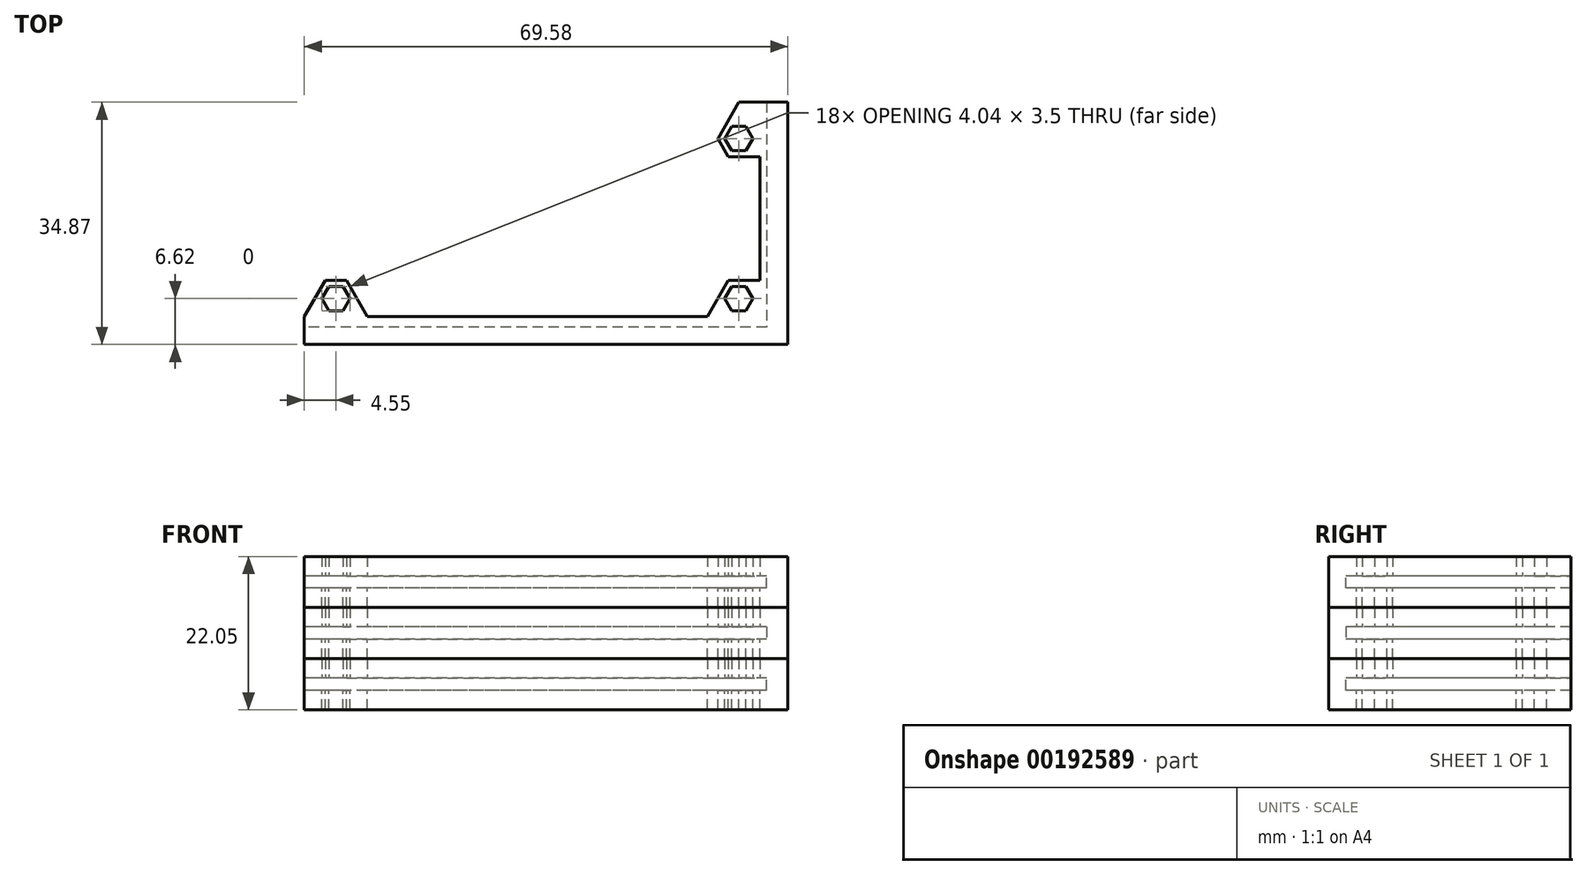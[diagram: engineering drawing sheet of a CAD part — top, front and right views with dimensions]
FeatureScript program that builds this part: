
annotation { "Feature Type Name" : "Feature", "Feature Type Description" : "" }
export const myFeature = defineFeature(function(context is Context, id is Id, definition is map)
    precondition{}
    {
        {
            var Q0;
            Q0=qCreatedBy(makeId("Top.planeOp"),FACE);
            var sketch = newSketch(context, id + "F0", { "sketchPlane" : qUnion([Q0])});
            skLineSegment(sketch, "E0.bottom", {"start": v(-29, 11.5) * mm, "end": v(29, 11.5) * mm, "construction": true});
            skLineSegment(sketch, "E0.top", {"start": v(-29, -11.5) * mm, "end": v(29, -11.5) * mm, "construction": true});
            skLineSegment(sketch, "E0.left", {"start": v(-29, 11.5) * mm, "end": v(-29, -11.5) * mm, "construction": true});
            skLineSegment(sketch, "E0.right", {"start": v(29, 11.5) * mm, "end": v(29, -11.5) * mm, "construction": true});
            skLineSegment(sketch, "E1", {"start": v(0, 11.5) * mm, "end": v(0, -11.5) * mm, "construction": true});
            skCircle(sketch, "E2.cCircle", {"center": v(-29, 11.5) * mm, "radius": 2.62 * mm, "construction": true});
            skLineSegment(sketch, "E2.0", {"start": v(-27.48, 14.12) * mm, "end": v(-25.97, 11.5) * mm});
            skLineSegment(sketch, "E2.1", {"start": v(-25.97, 11.5) * mm, "end": v(-27.48, 8.88) * mm});
            skLineSegment(sketch, "E2.2", {"start": v(-27.48, 8.87) * mm, "end": v(-30.52, 8.87) * mm});
            skLineSegment(sketch, "E2.3", {"start": v(-30.52, 8.88) * mm, "end": v(-32.03, 11.5) * mm});
            skLineSegment(sketch, "E2.4", {"start": v(-32.03, 11.5) * mm, "end": v(-30.52, 14.13) * mm});
            skLineSegment(sketch, "E2.5", {"start": v(-30.52, 14.13) * mm, "end": v(-27.48, 14.13) * mm});
            skLineSegment(sketch, "E3", {"start": v(-29, 0) * mm, "end": v(29, 0) * mm, "construction": true});
            skLineSegment(sketch, "E4.MirrorCS", {"start": v(-27.48, -14.12) * mm, "end": v(-25.97, -11.5) * mm});
            skLineSegment(sketch, "E5.MirrorCS", {"start": v(-25.97, -11.5) * mm, "end": v(-27.48, -8.88) * mm});
            skLineSegment(sketch, "E6.MirrorCS", {"start": v(-27.48, -8.87) * mm, "end": v(-30.52, -8.87) * mm});
            skLineSegment(sketch, "E7.MirrorCS", {"start": v(-30.52, -8.88) * mm, "end": v(-32.03, -11.5) * mm});
            skLineSegment(sketch, "E8.MirrorCS", {"start": v(-30.52, -14.12) * mm, "end": v(-27.48, -14.12) * mm});
            skLineSegment(sketch, "E9.MirrorCS", {"start": v(-32.03, -11.5) * mm, "end": v(-30.52, -14.13) * mm});
            skLineSegment(sketch, "E10.MirrorCS", {"start": v(30.52, -8.87) * mm, "end": v(32.03, -11.5) * mm});
            skLineSegment(sketch, "E11.MirrorCS", {"start": v(32.03, -11.5) * mm, "end": v(30.52, -14.12) * mm});
            skLineSegment(sketch, "E12.MirrorCS", {"start": v(30.52, -14.12) * mm, "end": v(27.48, -14.12) * mm});
            skLineSegment(sketch, "E13.MirrorCS", {"start": v(27.48, -14.12) * mm, "end": v(25.97, -11.5) * mm});
            skLineSegment(sketch, "E14.MirrorCS", {"start": v(25.97, -11.5) * mm, "end": v(27.48, -8.87) * mm});
            skLineSegment(sketch, "E15.MirrorCS", {"start": v(27.48, -8.87) * mm, "end": v(30.52, -8.87) * mm});
            skLineSegment(sketch, "E16.MirrorCS", {"start": v(30.52, 8.87) * mm, "end": v(32.03, 11.5) * mm});
            skLineSegment(sketch, "E17.MirrorCS", {"start": v(32.03, 11.5) * mm, "end": v(30.52, 14.12) * mm});
            skLineSegment(sketch, "E18.MirrorCS", {"start": v(30.52, 14.13) * mm, "end": v(27.48, 14.13) * mm});
            skLineSegment(sketch, "E19.MirrorCS", {"start": v(27.48, 8.88) * mm, "end": v(30.52, 8.88) * mm});
            skLineSegment(sketch, "E20.MirrorCS", {"start": v(27.48, 14.12) * mm, "end": v(25.97, 11.5) * mm});
            skLineSegment(sketch, "E21.MirrorCS", {"start": v(25.97, 11.5) * mm, "end": v(27.48, 8.87) * mm});
            skCircle(sketch, "E22.cCircle", {"center": v(-29, 11.5) * mm, "radius": 1.75 * mm, "construction": true});
            skLineSegment(sketch, "E22.0", {"start": v(-30.01, 13.25) * mm, "end": v(-27.99, 13.25) * mm});
            skLineSegment(sketch, "E22.1", {"start": v(-27.99, 13.25) * mm, "end": v(-26.98, 11.5) * mm});
            skLineSegment(sketch, "E22.2", {"start": v(-26.98, 11.5) * mm, "end": v(-27.99, 9.75) * mm});
            skLineSegment(sketch, "E22.3", {"start": v(-27.99, 9.75) * mm, "end": v(-30.01, 9.75) * mm});
            skLineSegment(sketch, "E22.4", {"start": v(-30.01, 9.75) * mm, "end": v(-31.02, 11.5) * mm});
            skLineSegment(sketch, "E22.5", {"start": v(-31.02, 11.5) * mm, "end": v(-30.01, 13.25) * mm});
            skLineSegment(sketch, "E23.MirrorCS", {"start": v(26.98, 11.5) * mm, "end": v(27.99, 9.75) * mm});
            skLineSegment(sketch, "E24.MirrorCS", {"start": v(27.99, 9.75) * mm, "end": v(30.01, 9.75) * mm});
            skLineSegment(sketch, "E25.MirrorCS", {"start": v(30.01, 9.75) * mm, "end": v(31.02, 11.5) * mm});
            skLineSegment(sketch, "E26.MirrorCS", {"start": v(31.02, 11.5) * mm, "end": v(30.01, 13.25) * mm});
            skLineSegment(sketch, "E27.MirrorCS", {"start": v(30.01, 13.25) * mm, "end": v(27.99, 13.25) * mm});
            skLineSegment(sketch, "E28.MirrorCS", {"start": v(27.99, 13.25) * mm, "end": v(26.98, 11.5) * mm});
            skLineSegment(sketch, "E29.MirrorCS", {"start": v(26.98, -11.5) * mm, "end": v(27.99, -9.75) * mm});
            skLineSegment(sketch, "E30.MirrorCS", {"start": v(27.99, -9.75) * mm, "end": v(30.01, -9.75) * mm});
            skLineSegment(sketch, "E31.MirrorCS", {"start": v(30.01, -9.75) * mm, "end": v(31.02, -11.5) * mm});
            skLineSegment(sketch, "E32.MirrorCS", {"start": v(31.02, -11.5) * mm, "end": v(30.01, -13.25) * mm});
            skLineSegment(sketch, "E33.MirrorCS", {"start": v(30.01, -13.25) * mm, "end": v(27.99, -13.25) * mm});
            skLineSegment(sketch, "E34.MirrorCS", {"start": v(27.99, -13.25) * mm, "end": v(26.98, -11.5) * mm});
            skLineSegment(sketch, "E35.MirrorCS", {"start": v(-31.02, -11.5) * mm, "end": v(-30.01, -13.25) * mm});
            skLineSegment(sketch, "E36.MirrorCS", {"start": v(-30.01, -9.75) * mm, "end": v(-31.02, -11.5) * mm});
            skLineSegment(sketch, "E37.MirrorCS", {"start": v(-27.99, -9.75) * mm, "end": v(-30.01, -9.75) * mm});
            skLineSegment(sketch, "E38.MirrorCS", {"start": v(-26.98, -11.5) * mm, "end": v(-27.99, -9.75) * mm});
            skLineSegment(sketch, "E39.MirrorCS", {"start": v(-30.01, -13.25) * mm, "end": v(-27.99, -13.25) * mm});
            skLineSegment(sketch, "E40.MirrorCS", {"start": v(-27.99, -13.25) * mm, "end": v(-26.98, -11.5) * mm});
            skLineSegment(sketch, "E41.bottom", {"start": v(-32.5, 15.12) * mm, "end": v(32.5, 15.13) * mm});
            skLineSegment(sketch, "E41.top", {"start": v(-32.5, -15.13) * mm, "end": v(32.5, -15.13) * mm});
            skLineSegment(sketch, "E41.left", {"start": v(-32.5, 15.12) * mm, "end": v(-32.5, -15.13) * mm});
            skLineSegment(sketch, "E41.right", {"start": v(32.5, 15.13) * mm, "end": v(32.5, -15.13) * mm});
            skLineSegment(sketch, "E42", {"start": v(32.5, 15.13) * mm, "end": v(-32.5, -15.13) * mm, "construction": true});
            skPoint(sketch, "E43", {"position": v(0, 0) * mm});
            skSolve(sketch);
        }
        {
            var Q0;
            Q0=qCreatedBy(makeId("Top.planeOp"),FACE);
            var sketch = newSketch(context, id + "F1", { "sketchPlane" : qUnion([Q0])});
            skLineSegment(sketch, "E44.0", {"start": v(-30.52, -8.88) * mm, "end": v(-32.03, -11.5) * mm});
            skLineSegment(sketch, "E44.1", {"start": v(-27.48, -8.87) * mm, "end": v(-30.52, -8.87) * mm});
            skLineSegment(sketch, "E44.2", {"start": v(-25.97, -11.5) * mm, "end": v(-27.48, -8.88) * mm});
            skLineSegment(sketch, "E45.0", {"start": v(25.97, -11.5) * mm, "end": v(27.48, -8.87) * mm});
            skLineSegment(sketch, "E45.1", {"start": v(27.48, -8.87) * mm, "end": v(30.52, -8.87) * mm});
            skLineSegment(sketch, "E46.0", {"start": v(25.97, 11.5) * mm, "end": v(27.48, 8.87) * mm});
            skLineSegment(sketch, "E46.1", {"start": v(27.48, 8.88) * mm, "end": v(30.52, 8.88) * mm});
            skLineSegment(sketch, "E47.0", {"start": v(27.48, 14.12) * mm, "end": v(25.97, 11.5) * mm});
            skLineSegment(sketch, "E48", {"start": v(30.52, 8.88) * mm, "end": v(32.03, 8.88) * mm});
            skLineSegment(sketch, "E49", {"start": v(32.03, 8.88) * mm, "end": v(32.03, -8.87) * mm});
            skLineSegment(sketch, "E50", {"start": v(32.03, -8.87) * mm, "end": v(30.52, -8.87) * mm});
            skLineSegment(sketch, "E51", {"start": v(36.03, 16.75) * mm, "end": v(36.03, -18.12) * mm});
            skLineSegment(sketch, "E52", {"start": v(36.03, -18.12) * mm, "end": v(-33.55, -18.13) * mm});
            skLineSegment(sketch, "E53", {"start": v(32.03, 11.5) * mm, "end": v(32.03, 8.88) * mm, "construction": true});
            skLineSegment(sketch, "E54", {"start": v(-25.97, -11.5) * mm, "end": v(-24.45, -14.12) * mm});
            skLineSegment(sketch, "E55", {"start": v(-24.45, -14.12) * mm, "end": v(24.45, -14.12) * mm});
            skLineSegment(sketch, "E56", {"start": v(24.45, -14.12) * mm, "end": v(25.97, -11.5) * mm});
            skLineSegment(sketch, "E57", {"start": v(-24.45, -14.12) * mm, "end": v(-27.48, -14.12) * mm, "construction": true});
            skLineSegment(sketch, "E58.0", {"start": v(-30.01, -9.75) * mm, "end": v(-31.02, -11.5) * mm});
            skLineSegment(sketch, "E58.1", {"start": v(-31.02, -11.5) * mm, "end": v(-30.01, -13.25) * mm});
            skLineSegment(sketch, "E58.2", {"start": v(-30.01, -13.25) * mm, "end": v(-27.99, -13.25) * mm});
            skLineSegment(sketch, "E58.3", {"start": v(-27.99, -13.25) * mm, "end": v(-26.98, -11.5) * mm});
            skLineSegment(sketch, "E58.4", {"start": v(-26.98, -11.5) * mm, "end": v(-27.99, -9.75) * mm});
            skLineSegment(sketch, "E58.5", {"start": v(-27.99, -9.75) * mm, "end": v(-30.01, -9.75) * mm});
            skLineSegment(sketch, "E59.0", {"start": v(26.98, -11.5) * mm, "end": v(27.99, -9.75) * mm});
            skLineSegment(sketch, "E59.1", {"start": v(27.99, -13.25) * mm, "end": v(26.98, -11.5) * mm});
            skLineSegment(sketch, "E59.2", {"start": v(30.01, -13.25) * mm, "end": v(27.99, -13.25) * mm});
            skLineSegment(sketch, "E59.3", {"start": v(31.02, -11.5) * mm, "end": v(30.01, -13.25) * mm});
            skLineSegment(sketch, "E59.4", {"start": v(30.01, -9.75) * mm, "end": v(31.02, -11.5) * mm});
            skLineSegment(sketch, "E59.5", {"start": v(27.99, -9.75) * mm, "end": v(30.01, -9.75) * mm});
            skLineSegment(sketch, "E59.6", {"start": v(27.99, 9.75) * mm, "end": v(30.01, 9.75) * mm});
            skLineSegment(sketch, "E59.7", {"start": v(26.98, 11.5) * mm, "end": v(27.99, 9.75) * mm});
            skLineSegment(sketch, "E59.8", {"start": v(27.99, 13.25) * mm, "end": v(26.98, 11.5) * mm});
            skLineSegment(sketch, "E59.9", {"start": v(30.01, 13.25) * mm, "end": v(27.99, 13.25) * mm});
            skPoint(sketch, "E59.10", {"position": v(31.02, 11.5) * mm});
            skLineSegment(sketch, "E59.11", {"start": v(30.01, 9.75) * mm, "end": v(31.02, 11.5) * mm});
            skLineSegment(sketch, "E59.12", {"start": v(31.02, 11.5) * mm, "end": v(30.01, 13.25) * mm});
            skLineSegment(sketch, "E60", {"start": v(-32.03, -11.5) * mm, "end": v(-33.55, -14.12) * mm});
            skLineSegment(sketch, "E61", {"start": v(-33.55, -14.13) * mm, "end": v(-33.55, -18.12) * mm});
            skLineSegment(sketch, "E62", {"start": v(27.48, 14.12) * mm, "end": v(29, 16.75) * mm});
            skLineSegment(sketch, "E63", {"start": v(36.03, 16.75) * mm, "end": v(29, 16.75) * mm});
            skSolve(sketch);
        }
        {
            var Q0;
            Q0=qSketchRegion(id+"F1",true);
            extrude(context, id + "F2", {"entities" : qUnion([Q0]), "depth" : 2.8 * mm});
        }
        {
            var Q0;
            Q0=makeQuery(id+"F2.opExtrude","CAP_FACE",FACE,{"disambiguationData":[OSD([sQuery(id+"F1.wireOp",EDGE,"E44.0"),sQuery(id+"F1.wireOp",EDGE,"E44.1"),sQuery(id+"F1.wireOp",EDGE,"E44.2"),sQuery(id+"F1.wireOp",EDGE,"E45.0"),sQuery(id+"F1.wireOp",EDGE,"E45.1"),sQuery(id+"F1.wireOp",EDGE,"E46.0"),sQuery(id+"F1.wireOp",EDGE,"E46.1"),sQuery(id+"F1.wireOp",EDGE,"E47.0"),sQuery(id+"F1.wireOp",EDGE,"E48"),sQuery(id+"F1.wireOp",EDGE,"E49"),sQuery(id+"F1.wireOp",EDGE,"E50"),sQuery(id+"F1.wireOp",EDGE,"E51"),sQuery(id+"F1.wireOp",EDGE,"E52"),sQuery(id+"F1.wireOp",EDGE,"E54"),sQuery(id+"F1.wireOp",EDGE,"E55"),sQuery(id+"F1.wireOp",EDGE,"E56"),sQuery(id+"F1.wireOp",EDGE,"E58.0"),sQuery(id+"F1.wireOp",EDGE,"E58.1"),sQuery(id+"F1.wireOp",EDGE,"E58.2"),sQuery(id+"F1.wireOp",EDGE,"E58.3"),sQuery(id+"F1.wireOp",EDGE,"E58.4"),sQuery(id+"F1.wireOp",EDGE,"E58.5"),sQuery(id+"F1.wireOp",EDGE,"E59.0"),sQuery(id+"F1.wireOp",EDGE,"E59.1"),sQuery(id+"F1.wireOp",EDGE,"E59.2"),sQuery(id+"F1.wireOp",EDGE,"E59.3"),sQuery(id+"F1.wireOp",EDGE,"E59.4"),sQuery(id+"F1.wireOp",EDGE,"E59.5"),sQuery(id+"F1.wireOp",EDGE,"E59.6"),sQuery(id+"F1.wireOp",EDGE,"E59.7"),sQuery(id+"F1.wireOp",EDGE,"E59.8"),sQuery(id+"F1.wireOp",EDGE,"E59.9"),sQuery(id+"F1.wireOp",EDGE,"E59.11"),sQuery(id+"F1.wireOp",EDGE,"E59.12"),sQuery(id+"F1.wireOp",EDGE,"E60"),sQuery(id+"F1.wireOp",EDGE,"E61"),sQuery(id+"F1.wireOp",EDGE,"E62"),sQuery(id+"F1.wireOp",EDGE,"E63")])],"isStart":true});
            var sketch = newSketch(context, id + "F3", { "sketchPlane" : qUnion([Q0])});
            skLineSegment(sketch, "E64", {"start": v(-33.55, 18.12) * mm, "end": v(36.03, 18.12) * mm});
            skLineSegment(sketch, "E65", {"start": v(36.03, 18.12) * mm, "end": v(36.03, -16.75) * mm});
            skLineSegment(sketch, "E66", {"start": v(36.03, -16.75) * mm, "end": v(33, -16.75) * mm});
            skLineSegment(sketch, "E67", {"start": v(33, -16.75) * mm, "end": v(33, 15.63) * mm});
            skLineSegment(sketch, "E68", {"start": v(33, 15.63) * mm, "end": v(-33.55, 15.62) * mm});
            skLineSegment(sketch, "E69", {"start": v(-33.55, 15.62) * mm, "end": v(-33.55, 18.12) * mm});
            skSolve(sketch);
        }
        {
            var Q0;
            Q0=qSketchRegion(id+"F3",true);
            extrude(context, id + "F4", {"entities" : qUnion([Q0]), "operationType" : NewBodyOperationType.ADD, "depth" : 1.75 * mm});
        }
        {
            var Q0;
            Q0=makeQuery(id+"F4.opExtrude","CAP_FACE",FACE,{"disambiguationData":[OSD([sQuery(id+"F3.wireOp",EDGE,"E64"),sQuery(id+"F3.wireOp",EDGE,"E65"),sQuery(id+"F3.wireOp",EDGE,"E66"),sQuery(id+"F3.wireOp",EDGE,"E67"),sQuery(id+"F3.wireOp",EDGE,"E68"),sQuery(id+"F3.wireOp",EDGE,"E69")])],"isStart":false});
            var sketch = newSketch(context, id + "F5", { "sketchPlane" : qUnion([Q0])});
            skLineSegment(sketch, "E70.0.0", {"start": v(-27.48, 8.87) * mm, "end": v(-30.52, 8.87) * mm});
            skLineSegment(sketch, "E70.0.1", {"start": v(-30.52, 8.88) * mm, "end": v(-33.55, 14.12) * mm});
            skLineSegment(sketch, "E70.0.2", {"start": v(-33.55, 14.13) * mm, "end": v(-33.55, 18.12) * mm});
            skLineSegment(sketch, "E70.0.3", {"start": v(-33.55, 18.13) * mm, "end": v(36.03, 18.12) * mm});
            skLineSegment(sketch, "E70.0.4", {"start": v(36.03, 18.12) * mm, "end": v(36.03, -16.75) * mm});
            skLineSegment(sketch, "E70.0.5", {"start": v(36.03, -16.75) * mm, "end": v(29, -16.75) * mm});
            skLineSegment(sketch, "E70.0.6", {"start": v(29, -16.75) * mm, "end": v(25.97, -11.5) * mm});
            skLineSegment(sketch, "E70.0.7", {"start": v(25.97, -11.5) * mm, "end": v(27.48, -8.88) * mm});
            skLineSegment(sketch, "E70.0.8", {"start": v(27.48, -8.88) * mm, "end": v(32.03, -8.88) * mm});
            skLineSegment(sketch, "E70.0.9", {"start": v(32.03, -8.88) * mm, "end": v(32.03, 8.87) * mm});
            skLineSegment(sketch, "E70.0.10", {"start": v(32.03, 8.87) * mm, "end": v(27.48, 8.87) * mm});
            skLineSegment(sketch, "E70.0.11", {"start": v(27.48, 8.87) * mm, "end": v(24.45, 14.12) * mm});
            skLineSegment(sketch, "E70.0.12", {"start": v(24.45, 14.12) * mm, "end": v(-24.45, 14.12) * mm});
            skLineSegment(sketch, "E70.0.13", {"start": v(-24.45, 14.12) * mm, "end": v(-27.48, 8.87) * mm});
            skLineSegment(sketch, "E71.0", {"start": v(-30.01, 9.75) * mm, "end": v(-31.02, 11.5) * mm});
            skLineSegment(sketch, "E71.1", {"start": v(-31.02, 11.5) * mm, "end": v(-30.01, 13.25) * mm});
            skLineSegment(sketch, "E71.2", {"start": v(-30.01, 13.25) * mm, "end": v(-27.99, 13.25) * mm});
            skLineSegment(sketch, "E71.3", {"start": v(-27.99, 13.25) * mm, "end": v(-26.98, 11.5) * mm});
            skLineSegment(sketch, "E71.4", {"start": v(-26.98, 11.5) * mm, "end": v(-27.99, 9.75) * mm});
            skLineSegment(sketch, "E71.5", {"start": v(-27.99, 9.75) * mm, "end": v(-30.01, 9.75) * mm});
            skLineSegment(sketch, "E71.6", {"start": v(27.99, 13.25) * mm, "end": v(26.98, 11.5) * mm});
            skLineSegment(sketch, "E71.7", {"start": v(26.98, 11.5) * mm, "end": v(27.99, 9.75) * mm});
            skLineSegment(sketch, "E71.8", {"start": v(27.99, 9.75) * mm, "end": v(30.01, 9.75) * mm});
            skLineSegment(sketch, "E71.9", {"start": v(30.01, 9.75) * mm, "end": v(31.02, 11.5) * mm});
            skLineSegment(sketch, "E71.10", {"start": v(31.02, 11.5) * mm, "end": v(30.01, 13.25) * mm});
            skLineSegment(sketch, "E71.11", {"start": v(30.01, 13.25) * mm, "end": v(27.99, 13.25) * mm});
            skLineSegment(sketch, "E71.12", {"start": v(26.98, -11.5) * mm, "end": v(27.99, -9.75) * mm});
            skLineSegment(sketch, "E71.13", {"start": v(27.99, -13.25) * mm, "end": v(26.98, -11.5) * mm});
            skLineSegment(sketch, "E71.14", {"start": v(30.01, -13.25) * mm, "end": v(27.99, -13.25) * mm});
            skLineSegment(sketch, "E71.15", {"start": v(31.02, -11.5) * mm, "end": v(30.01, -13.25) * mm});
            skLineSegment(sketch, "E71.16", {"start": v(30.01, -9.75) * mm, "end": v(31.02, -11.5) * mm});
            skLineSegment(sketch, "E71.17", {"start": v(27.99, -9.75) * mm, "end": v(30.01, -9.75) * mm});
            skSolve(sketch);
        }
        {
            var Q0;
            Q0=qSketchRegion(id+"F5",true);
            extrude(context, id + "F6", {"entities" : qUnion([Q0]), "operationType" : NewBodyOperationType.ADD, "depth" : 2.8 * mm});
        }
        {
            var Q0;
            Q0=makeQuery(id+"F2.opExtrude","SWEPT_BODY",BODY,{"disambiguationData":[OSD([sQuery(id+"F1.wireOp",EDGE,"E44.0"),sQuery(id+"F1.wireOp",EDGE,"E44.1"),sQuery(id+"F1.wireOp",EDGE,"E44.2"),sQuery(id+"F1.wireOp",EDGE,"E45.0"),sQuery(id+"F1.wireOp",EDGE,"E45.1"),sQuery(id+"F1.wireOp",EDGE,"E46.0"),sQuery(id+"F1.wireOp",EDGE,"E46.1"),sQuery(id+"F1.wireOp",EDGE,"E47.0"),sQuery(id+"F1.wireOp",EDGE,"E48"),sQuery(id+"F1.wireOp",EDGE,"E49"),sQuery(id+"F1.wireOp",EDGE,"E50"),sQuery(id+"F1.wireOp",EDGE,"E51"),sQuery(id+"F1.wireOp",EDGE,"E52"),sQuery(id+"F1.wireOp",EDGE,"E54"),sQuery(id+"F1.wireOp",EDGE,"E55"),sQuery(id+"F1.wireOp",EDGE,"E56"),sQuery(id+"F1.wireOp",EDGE,"E58.0"),sQuery(id+"F1.wireOp",EDGE,"E58.1"),sQuery(id+"F1.wireOp",EDGE,"E58.2"),sQuery(id+"F1.wireOp",EDGE,"E58.3"),sQuery(id+"F1.wireOp",EDGE,"E58.4"),sQuery(id+"F1.wireOp",EDGE,"E58.5"),sQuery(id+"F1.wireOp",EDGE,"E59.0"),sQuery(id+"F1.wireOp",EDGE,"E59.1"),sQuery(id+"F1.wireOp",EDGE,"E59.2"),sQuery(id+"F1.wireOp",EDGE,"E59.3"),sQuery(id+"F1.wireOp",EDGE,"E59.4"),sQuery(id+"F1.wireOp",EDGE,"E59.5"),sQuery(id+"F1.wireOp",EDGE,"E59.6"),sQuery(id+"F1.wireOp",EDGE,"E59.7"),sQuery(id+"F1.wireOp",EDGE,"E59.8"),sQuery(id+"F1.wireOp",EDGE,"E59.9"),sQuery(id+"F1.wireOp",EDGE,"E59.11"),sQuery(id+"F1.wireOp",EDGE,"E59.12"),sQuery(id+"F1.wireOp",EDGE,"E60"),sQuery(id+"F1.wireOp",EDGE,"E61"),sQuery(id+"F1.wireOp",EDGE,"E62"),sQuery(id+"F1.wireOp",EDGE,"E63")])]});
            var Q1;
            Q1=makeQuery(id+"F2.opExtrude","CAP_FACE",FACE,{"disambiguationData":[OSD([sQuery(id+"F1.wireOp",EDGE,"E44.0"),sQuery(id+"F1.wireOp",EDGE,"E44.1"),sQuery(id+"F1.wireOp",EDGE,"E44.2"),sQuery(id+"F1.wireOp",EDGE,"E45.0"),sQuery(id+"F1.wireOp",EDGE,"E45.1"),sQuery(id+"F1.wireOp",EDGE,"E46.0"),sQuery(id+"F1.wireOp",EDGE,"E46.1"),sQuery(id+"F1.wireOp",EDGE,"E47.0"),sQuery(id+"F1.wireOp",EDGE,"E48"),sQuery(id+"F1.wireOp",EDGE,"E49"),sQuery(id+"F1.wireOp",EDGE,"E50"),sQuery(id+"F1.wireOp",EDGE,"E51"),sQuery(id+"F1.wireOp",EDGE,"E52"),sQuery(id+"F1.wireOp",EDGE,"E54"),sQuery(id+"F1.wireOp",EDGE,"E55"),sQuery(id+"F1.wireOp",EDGE,"E56"),sQuery(id+"F1.wireOp",EDGE,"E58.0"),sQuery(id+"F1.wireOp",EDGE,"E58.1"),sQuery(id+"F1.wireOp",EDGE,"E58.2"),sQuery(id+"F1.wireOp",EDGE,"E58.3"),sQuery(id+"F1.wireOp",EDGE,"E58.4"),sQuery(id+"F1.wireOp",EDGE,"E58.5"),sQuery(id+"F1.wireOp",EDGE,"E59.0"),sQuery(id+"F1.wireOp",EDGE,"E59.1"),sQuery(id+"F1.wireOp",EDGE,"E59.2"),sQuery(id+"F1.wireOp",EDGE,"E59.3"),sQuery(id+"F1.wireOp",EDGE,"E59.4"),sQuery(id+"F1.wireOp",EDGE,"E59.5"),sQuery(id+"F1.wireOp",EDGE,"E59.6"),sQuery(id+"F1.wireOp",EDGE,"E59.7"),sQuery(id+"F1.wireOp",EDGE,"E59.8"),sQuery(id+"F1.wireOp",EDGE,"E59.9"),sQuery(id+"F1.wireOp",EDGE,"E59.11"),sQuery(id+"F1.wireOp",EDGE,"E59.12"),sQuery(id+"F1.wireOp",EDGE,"E60"),sQuery(id+"F1.wireOp",EDGE,"E61"),sQuery(id+"F1.wireOp",EDGE,"E62"),sQuery(id+"F1.wireOp",EDGE,"E63")])],"isStart":false});
            mirror(context, id + "F7", {"entities" : qUnion([Q0]), "mirrorPlane" : qUnion([Q1])});
        }
        {
            var Q0;
            Q0=makeQuery(id+"F7.opPattern","COPY",BODY,{"derivedFrom":makeQuery(id+"F2.opExtrude","SWEPT_BODY",BODY,{"disambiguationData":[OSD([sQuery(id+"F1.wireOp",EDGE,"E44.0"),sQuery(id+"F1.wireOp",EDGE,"E44.1"),sQuery(id+"F1.wireOp",EDGE,"E44.2"),sQuery(id+"F1.wireOp",EDGE,"E45.0"),sQuery(id+"F1.wireOp",EDGE,"E45.1"),sQuery(id+"F1.wireOp",EDGE,"E46.0"),sQuery(id+"F1.wireOp",EDGE,"E46.1"),sQuery(id+"F1.wireOp",EDGE,"E47.0"),sQuery(id+"F1.wireOp",EDGE,"E48"),sQuery(id+"F1.wireOp",EDGE,"E49"),sQuery(id+"F1.wireOp",EDGE,"E50"),sQuery(id+"F1.wireOp",EDGE,"E51"),sQuery(id+"F1.wireOp",EDGE,"E52"),sQuery(id+"F1.wireOp",EDGE,"E54"),sQuery(id+"F1.wireOp",EDGE,"E55"),sQuery(id+"F1.wireOp",EDGE,"E56"),sQuery(id+"F1.wireOp",EDGE,"E58.0"),sQuery(id+"F1.wireOp",EDGE,"E58.1"),sQuery(id+"F1.wireOp",EDGE,"E58.2"),sQuery(id+"F1.wireOp",EDGE,"E58.3"),sQuery(id+"F1.wireOp",EDGE,"E58.4"),sQuery(id+"F1.wireOp",EDGE,"E58.5"),sQuery(id+"F1.wireOp",EDGE,"E59.0"),sQuery(id+"F1.wireOp",EDGE,"E59.1"),sQuery(id+"F1.wireOp",EDGE,"E59.2"),sQuery(id+"F1.wireOp",EDGE,"E59.3"),sQuery(id+"F1.wireOp",EDGE,"E59.4"),sQuery(id+"F1.wireOp",EDGE,"E59.5"),sQuery(id+"F1.wireOp",EDGE,"E59.6"),sQuery(id+"F1.wireOp",EDGE,"E59.7"),sQuery(id+"F1.wireOp",EDGE,"E59.8"),sQuery(id+"F1.wireOp",EDGE,"E59.9"),sQuery(id+"F1.wireOp",EDGE,"E59.11"),sQuery(id+"F1.wireOp",EDGE,"E59.12"),sQuery(id+"F1.wireOp",EDGE,"E60"),sQuery(id+"F1.wireOp",EDGE,"E61"),sQuery(id+"F1.wireOp",EDGE,"E62"),sQuery(id+"F1.wireOp",EDGE,"E63")])]}),"instanceName":"1"});
            var Q1;
            Q1=makeQuery(id+"F7.opPattern","COPY",FACE,{"derivedFrom":makeQuery(id+"F6.opExtrude","CAP_FACE",FACE,{"disambiguationData":[OSD([sQuery(id+"F5.wireOp",EDGE,"E70.0.0"),sQuery(id+"F5.wireOp",EDGE,"E70.0.1"),sQuery(id+"F5.wireOp",EDGE,"E70.0.2"),sQuery(id+"F5.wireOp",EDGE,"E70.0.3"),sQuery(id+"F5.wireOp",EDGE,"E70.0.4"),sQuery(id+"F5.wireOp",EDGE,"E70.0.5"),sQuery(id+"F5.wireOp",EDGE,"E70.0.6"),sQuery(id+"F5.wireOp",EDGE,"E70.0.7"),sQuery(id+"F5.wireOp",EDGE,"E70.0.8"),sQuery(id+"F5.wireOp",EDGE,"E70.0.9"),sQuery(id+"F5.wireOp",EDGE,"E70.0.10"),sQuery(id+"F5.wireOp",EDGE,"E70.0.11"),sQuery(id+"F5.wireOp",EDGE,"E70.0.12"),sQuery(id+"F5.wireOp",EDGE,"E70.0.13"),sQuery(id+"F5.wireOp",EDGE,"E71.0"),sQuery(id+"F5.wireOp",EDGE,"E71.1"),sQuery(id+"F5.wireOp",EDGE,"E71.2"),sQuery(id+"F5.wireOp",EDGE,"E71.3"),sQuery(id+"F5.wireOp",EDGE,"E71.4"),sQuery(id+"F5.wireOp",EDGE,"E71.5"),sQuery(id+"F5.wireOp",EDGE,"E71.6"),sQuery(id+"F5.wireOp",EDGE,"E71.7"),sQuery(id+"F5.wireOp",EDGE,"E71.8"),sQuery(id+"F5.wireOp",EDGE,"E71.9"),sQuery(id+"F5.wireOp",EDGE,"E71.10"),sQuery(id+"F5.wireOp",EDGE,"E71.11"),sQuery(id+"F5.wireOp",EDGE,"E71.12"),sQuery(id+"F5.wireOp",EDGE,"E71.13"),sQuery(id+"F5.wireOp",EDGE,"E71.14"),sQuery(id+"F5.wireOp",EDGE,"E71.15"),sQuery(id+"F5.wireOp",EDGE,"E71.16"),sQuery(id+"F5.wireOp",EDGE,"E71.17")])],"isStart":false}),"instanceName":"1"});
            mirror(context, id + "F8", {"entities" : qUnion([Q0]), "mirrorPlane" : qUnion([Q1])});
        }
    });
